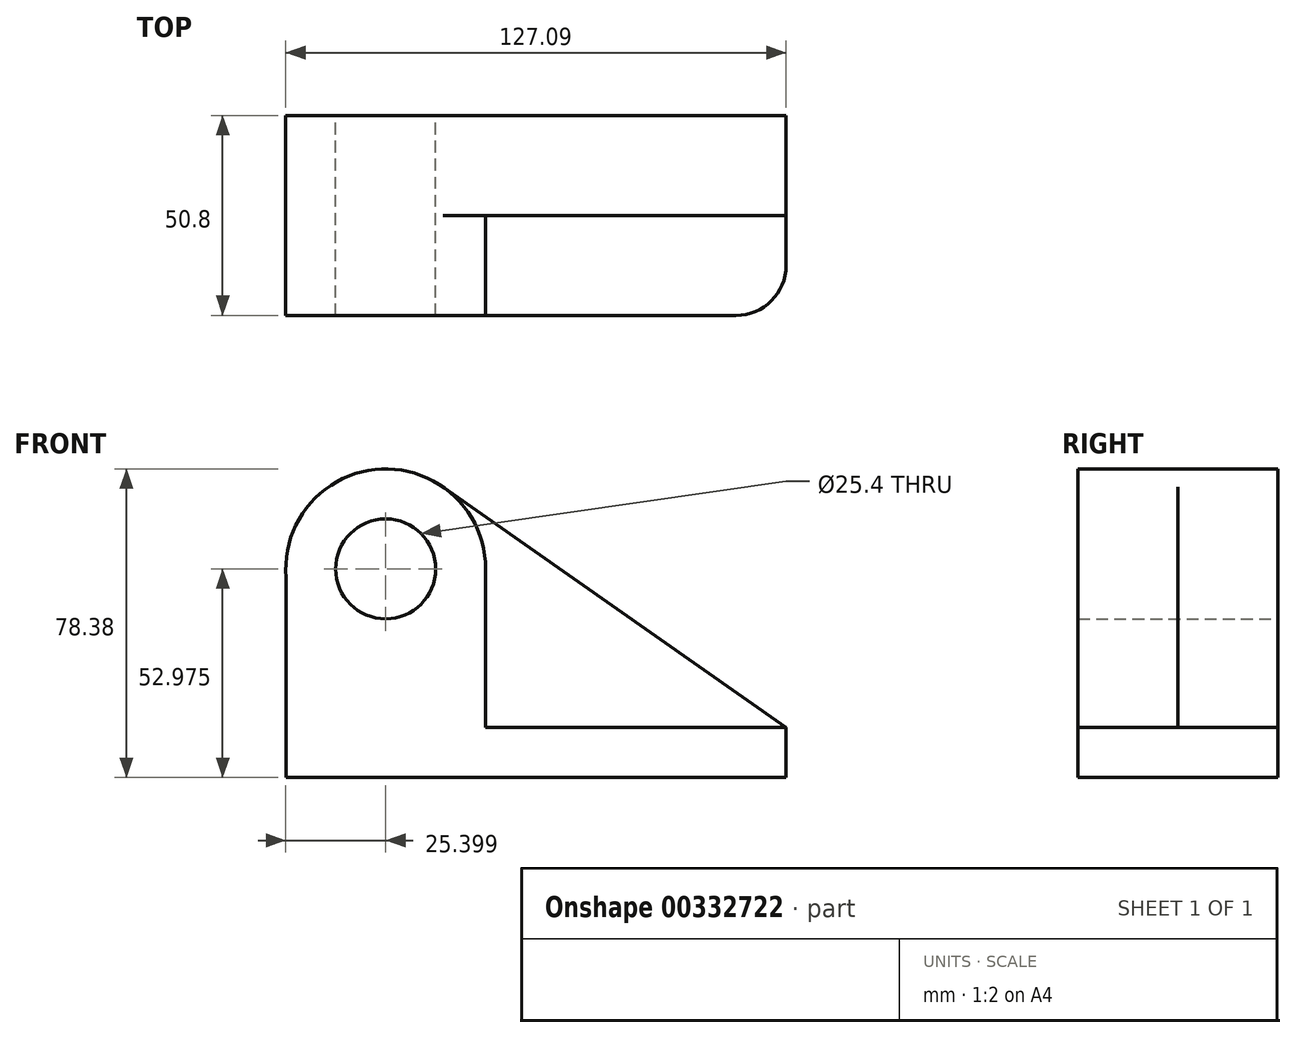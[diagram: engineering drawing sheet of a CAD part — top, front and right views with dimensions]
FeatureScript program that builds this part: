
annotation { "Feature Type Name" : "Feature", "Feature Type Description" : "" }
export const myFeature = defineFeature(function(context is Context, id is Id, definition is map)
    precondition{}
    {
        {
            var Q0;
            Q0=qCreatedBy(makeId("Front.planeOp"),FACE);
            var sketch = newSketch(context, id + "F0", { "sketchPlane" : qUnion([Q0])});
            skCircle(sketch, "E0", {"center": v(-50.3, 42.02) * mm, "radius": 12.7 * mm});
            skCircle(sketch, "E1", {"center": v(-50.3, 42.02) * mm, "radius": 25.4 * mm});
            skLineSegment(sketch, "E2", {"start": v(-75.6, 39.84) * mm, "end": v(-75.6, -10.96) * mm});
            skLineSegment(sketch, "E3", {"start": v(-75.6, -10.96) * mm, "end": v(51.4, -10.96) * mm});
            skLineSegment(sketch, "E4", {"start": v(51.4, -10.96) * mm, "end": v(51.4, 1.74) * mm});
            skLineSegment(sketch, "E5", {"start": v(51.4, 1.74) * mm, "end": v(-35.71, 62.81) * mm});
            skSolve(sketch);
        }
        {
            var Q0;
            Q0 = qSketchRegion(id + "F0", true);
            extrude(context, id + "F1", {"entities" : qUnion([Q0]), "depth" : 25.4 * mm});
        }
        {
            var Q0;
            Q0=makeQuery(id+"F1.opExtrude","CAP_FACE",FACE,{"disambiguationData":[OSD([sQuery(id+"F0.wireOp",EDGE,"E0"),sQuery(id+"F0.wireOp",EDGE,"E1"),sQuery(id+"F0.wireOp",EDGE,"E2"),sQuery(id+"F0.wireOp",EDGE,"E3"),sQuery(id+"F0.wireOp",EDGE,"E4"),sQuery(id+"F0.wireOp",EDGE,"E5")])],"isStart":false});
            var sketch = newSketch(context, id + "F2", { "sketchPlane" : qUnion([Q0])});
            skCircle(sketch, "E6", {"center": v(-50.3, 42.02) * mm, "radius": 12.7 * mm});
            skArc(sketch, "E7", {"start": v(-24.9, 42.02) * mm, "mid": v(-50.35, 67.42) * mm, "end": v(-75.7, 41.9) * mm});
            skLineSegment(sketch, "E8.bottom", {"start": v(51.4, 1.74) * mm, "end": v(-24.9, 1.74) * mm});
            skLineSegment(sketch, "E8.top", {"start": v(51.4, -10.96) * mm, "end": v(-75.6, -10.96) * mm});
            skLineSegment(sketch, "E8.left", {"start": v(51.4, 1.74) * mm, "end": v(51.4, -10.96) * mm});
            skLineSegment(sketch, "E8.right", {"start": v(-75.6, 1.74) * mm, "end": v(-75.6, -10.96) * mm});
            skLineSegment(sketch, "E9", {"start": v(-75.7, 42.02) * mm, "end": v(-75.6, 1.74) * mm});
            skLineSegment(sketch, "E10", {"start": v(-24.9, 42.02) * mm, "end": v(-24.9, 1.74) * mm});
            skPoint(sketch, "E11.orphan", {"position": v(-24.9, 0) * mm});
            skSolve(sketch);
        }
        {
            var Q0;
            Q0=makeQuery(id+"F2.imprint","IMPRINT",FACE,{"disambiguationData":[TD([[makeQuery(id+"F2.imprint","IMPRINT",EDGE,{"derivedFrom":sQuery(id+"F2.wireOp",EDGE,"E6")}),-1.0]])]});
            extrude(context, id + "F3", {"entities" : qUnion([Q0]), "operationType" : NewBodyOperationType.ADD, "depth" : 25.4 * mm});
        }
        {
            var Q0;
            Q0=makeQuery(id+"F3.opExtrude","CAP_EDGE",EDGE,{"disambiguationData":[OSD([sQuery(id+"F2.wireOp",EDGE,"E8.left")])],"isStart":false});
            fillet(context, id + "F4", {"entities" : qUnion([Q0]), "radius" : 12.7 * mm, "tangentPropagation" : true, "allowEdgeOverflow" : false});
        }
    });
